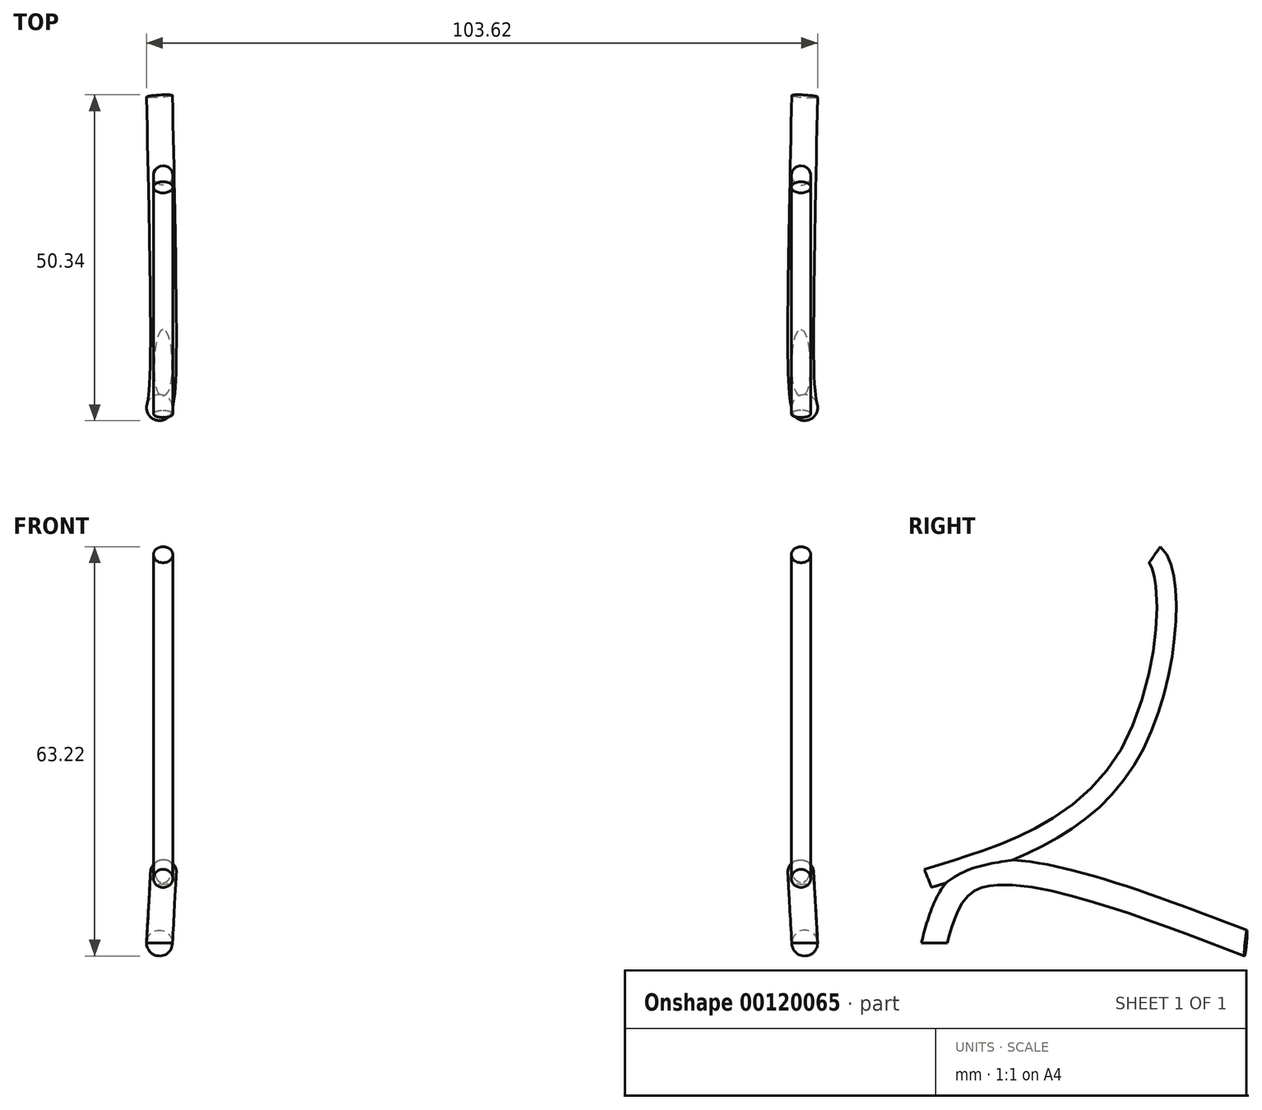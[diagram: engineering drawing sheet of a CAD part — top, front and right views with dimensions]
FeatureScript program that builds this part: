
annotation { "Feature Type Name" : "Feature", "Feature Type Description" : "" }
export const myFeature = defineFeature(function(context is Context, id is Id, definition is map)
    precondition{}
    {
        {
            var Q0;
            Q0=qCreatedBy(makeId("Front.planeOp"),FACE);
            var sketch = newSketch(context, id + "F0", { "sketchPlane" : qUnion([Q0])});
            skLineSegment(sketch, "E0", {"start": v(-49.25, 50) * mm, "end": v(50.75, 50) * mm});
            skSolve(sketch);
        }
        {
            var Q0;
            Q0=qCreatedBy(makeId("Right.planeOp"),FACE);
            var sketch = newSketch(context, id + "F1", { "sketchPlane" : qUnion([Q0])});
            skLineSegment(sketch, "E1", {"start": v(0, 50) * mm, "end": v(-35.01, 0) * mm});
            skSolve(sketch);
        }
        {
            var Q0;
            Q0=qCreatedBy(makeId("Front.planeOp"),FACE);
            var Q1;
            Q1=sQuery(id+"F1.wireOp",VERTEX,"E1.end");
            cPlane(context, id + "F2", {"entities" : qUnion([Q0, Q1]), "cplaneType" : CPlaneType.PLANE_POINT, "offset" : 25.4 * mm, "width" : 152.4 * mm, "height" : 152.4 * mm});
        }
        {
            var Q0;
            Q0=qCreatedBy(id+"F2.planeOp",FACE);
            var sketch = newSketch(context, id + "F3", { "sketchPlane" : qUnion([Q0])});
            skLineSegment(sketch, "E2", {"start": v(-49.25, 0) * mm, "end": v(50.75, 0) * mm});
            skLineSegment(sketch, "E3", {"start": v(-49.25, 50) * mm, "end": v(-49.25, 0) * mm, "construction": true});
            skLineSegment(sketch, "E4", {"start": v(50.75, 0) * mm, "end": v(50.75, 50) * mm, "construction": true});
            skSolve(sketch);
        }
        {
            var Q0;
            Q0=qCreatedBy(makeId("Top.planeOp"),FACE);
            cPlane(context, id + "F4", {"entities" : qUnion([Q0]), "cplaneType" : CPlaneType.OFFSET, "offset" : 10 * mm, "oppositeDirection" : true, "width" : 152.4 * mm, "height" : 152.4 * mm});
        }
        {
            var Q0;
            Q0=qCreatedBy(id+"F4.planeOp",FACE);
            var sketch = newSketch(context, id + "F5", { "sketchPlane" : qUnion([Q0])});
            skLineSegment(sketch, "E5", {"start": v(-49.81, -34.04) * mm, "end": v(-49.81, 14.07) * mm});
            skLineSegment(sketch, "E6", {"start": v(50.5, -33.36) * mm, "end": v(50.5, 14.07) * mm});
            skSolve(sketch);
        }
        {
            var Q0;
            Q0=sQuery(id+"F3.wireOp",VERTEX,"E3.end");
            var Q1;
            Q1=sQuery(id+"F5.wireOp",VERTEX,"E5.start");
            var Q2;
            Q2=sQuery(id+"F5.wireOp",VERTEX,"E5.end");
            cPlane(context, id + "F6", {"entities" : qUnion([Q0, Q1, Q2]), "cplaneType" : CPlaneType.THREE_POINT, "offset" : 25.4 * mm, "width" : 152.4 * mm, "height" : 152.4 * mm});
        }
        {
            var Q0;
            Q0=qCreatedBy(id+"F6.planeOp",FACE);
            var sketch = newSketch(context, id + "F7", { "sketchPlane" : qUnion([Q0])});
            skFitSpline(sketch, "E7", {"points": [v(34.04, -12.77) * mm, v(27.92, -2.6) * mm, v(-14.07, -12.77) * mm], "startDerivative": vector(-9.97, 36.87) * mm, "endDerivative": vector(-79.01, -30.14) * mm});
            skSolve(sketch);
        }
        {
            var Q0;
            Q0=qCreatedBy(id+"F4.planeOp",FACE);
            var sketch = newSketch(context, id + "F8", { "sketchPlane" : qUnion([Q0])});
            skCircle(sketch, "E8", {"center": v(-49.81, -34.04) * mm, "radius": 2 * mm});
            skSolve(sketch);
        }
        {
            var Q0;
            Q0=makeQuery(id+"F8.imprint","IMPRINT",FACE,{"disambiguationData":[TD([[makeQuery(id+"F8.imprint","IMPRINT",EDGE,{"derivedFrom":sQuery(id+"F8.wireOp",EDGE,"E8")}),1.0]])]});
            var Q1;
            Q1=sQuery(id+"F8.wireOp",EDGE,"E8");
            var Q2;
            Q2=sQuery(id+"F7.wireOp",EDGE,"E7");
            sweep(context, id + "F9", {"profiles" : qUnion([Q0]), "surfaceProfiles" : qUnion([Q1]), "path" : qUnion([Q2])});
        }
        {
            var Q0;
            Q0=sQuery(id+"F0.wireOp",VERTEX,"E0.start");
            var Q1;
            Q1=sQuery(id+"F3.wireOp",VERTEX,"E3.end");
            var Q2;
            Q2=sQuery(id+"F3.wireOp",VERTEX,"E3.start");
            cPlane(context, id + "F10", {"entities" : qUnion([Q0, Q1, Q2]), "cplaneType" : CPlaneType.THREE_POINT, "offset" : 25.4 * mm, "width" : 152.4 * mm, "height" : 152.4 * mm});
        }
        {
            var Q0;
            Q0=qCreatedBy(id+"F10.planeOp",FACE);
            var sketch = newSketch(context, id + "F11", { "sketchPlane" : qUnion([Q0])});
            skFitSpline(sketch, "E9", {"points": [v(-35.01, 0) * mm, v(-4.38, 18.37) * mm, v(0, 50) * mm], "startDerivative": vector(58.02, 17.74) * mm, "endDerivative": vector(-20.35, 16.94) * mm});
            skSolve(sketch);
        }
        {
            var Q0;
            Q0=sQuery(id+"F0.wireOp",VERTEX,"E0.start");
            var Q1;
            Q1=sQuery(id+"F11.wireOp",VERTEX,"E9.start");
            var Q2;
            Q2=sQuery(id+"F1.wireOp",VERTEX,"E1.start");
            cPlane(context, id + "F12", {"entities" : qUnion([Q0, Q1, Q2]), "cplaneType" : CPlaneType.THREE_POINT, "offset" : 25.4 * mm, "width" : 152.4 * mm, "height" : 152.4 * mm});
        }
        {
            var Q0;
            Q0=qCreatedBy(id+"F12.planeOp",FACE);
            var sketch = newSketch(context, id + "F13", { "sketchPlane" : qUnion([Q0])});
            skCircle(sketch, "E10", {"center": v(49.25, 40.96) * mm, "radius": 1.5 * mm});
            skSolve(sketch);
        }
        {
            var Q0;
            Q0=makeQuery(id+"F13.imprint","IMPRINT",FACE,{"disambiguationData":[TD([[makeQuery(id+"F13.imprint","IMPRINT",EDGE,{"derivedFrom":sQuery(id+"F13.wireOp",EDGE,"E10")}),1.0]])]});
            var Q1;
            Q1=sQuery(id+"F11.wireOp",EDGE,"E9");
            sweep(context, id + "F14", {"operationType" : NewBodyOperationType.ADD, "profiles" : qUnion([Q0]), "path" : qUnion([Q1])});
        }
        {
            var Q0;
            Q0=makeQuery(id+"F9.opSweep","SWEPT_BODY",BODY,{"disambiguationData":[OSD([sQuery(id+"F7.wireOp",EDGE,"E7"),sQuery(id+"F8.wireOp",EDGE,"E8")])]});
            var Q1;
            Q1=qCreatedBy(makeId("Right.planeOp"),FACE);
            mirror(context, id + "F15", {"entities" : qUnion([Q0]), "mirrorPlane" : qUnion([Q1])});
        }
    });
